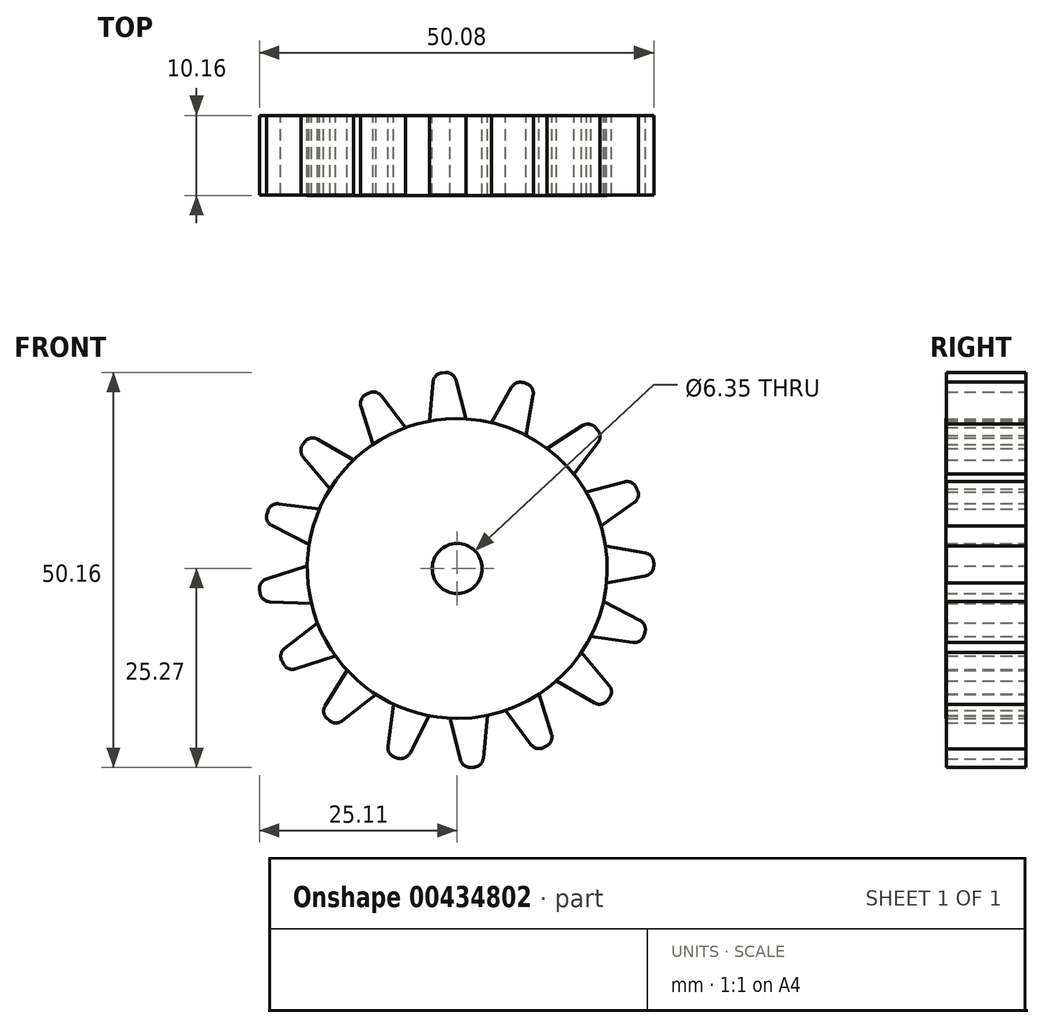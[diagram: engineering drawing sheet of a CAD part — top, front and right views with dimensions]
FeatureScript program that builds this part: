
annotation { "Feature Type Name" : "Feature", "Feature Type Description" : "" }
export const myFeature = defineFeature(function(context is Context, id is Id, definition is map)
    precondition{}
    {
        {
            var Q0;
            Q0=qCreatedBy(makeId("Front.planeOp"),FACE);
            var sketch = newSketch(context, id + "F0", { "sketchPlane" : qUnion([Q0])});
            skCircle(sketch, "E0", {"center": v(0, 0) * mm, "radius": 19.05 * mm});
            skCircle(sketch, "E1", {"center": v(0, 0) * mm, "radius": 3.18 * mm});
            skSolve(sketch);
        }
        {
            var Q0;
            Q0=makeQuery(id+"F0.imprint","IMPRINT",FACE,{"disambiguationData":[TD([[makeQuery(id+"F0.imprint","IMPRINT",EDGE,{"derivedFrom":sQuery(id+"F0.wireOp",EDGE,"E0")}),1.0]])]});
            extrude(context, id + "F1", {"entities" : qUnion([Q0]), "depth" : 3.8 * mm});
        }
        {
            var Q0;
            Q0=qCreatedBy(makeId("Front.planeOp"),FACE);
            var sketch = newSketch(context, id + "F2", { "sketchPlane" : qUnion([Q0])});
            skLineSegment(sketch, "E2", {"start": v(-45.5, 8.34) * mm, "end": v(-40.37, 8.34) * mm});
            skLineSegment(sketch, "E3", {"start": v(-45.5, 8.34) * mm, "end": v(-44.39, 14.6) * mm});
            skLineSegment(sketch, "E4", {"start": v(-43.14, 15.66) * mm, "end": v(-42.73, 15.66) * mm});
            skLineSegment(sketch, "E5", {"start": v(-41.48, 14.6) * mm, "end": v(-40.37, 8.34) * mm});
            skArc(sketch, "E6.filletArc", {"start": v(-43.14, 15.66) * mm, "mid": v(-43.95, 15.36) * mm, "end": v(-44.39, 14.6) * mm});
            skArc(sketch, "E7.filletArc", {"start": v(-41.48, 14.6) * mm, "mid": v(-41.91, 15.36) * mm, "end": v(-42.73, 15.66) * mm});
            skLineSegment(sketch, "E8", {"start": v(15.21, -9.97) * mm, "end": v(11.92, -13.9) * mm});
            skLineSegment(sketch, "E9", {"start": v(15.21, -9.97) * mm, "end": v(19.3, -14.84) * mm});
            skLineSegment(sketch, "E10", {"start": v(19.3, -16.48) * mm, "end": v(19.04, -16.8) * mm});
            skLineSegment(sketch, "E11", {"start": v(17.43, -17.07) * mm, "end": v(11.92, -13.9) * mm});
            skArc(sketch, "E12.filletArc", {"start": v(19.3, -16.48) * mm, "mid": v(19.6, -15.66) * mm, "end": v(19.3, -14.84) * mm});
            skArc(sketch, "E13.filletArc", {"start": v(17.43, -17.07) * mm, "mid": v(18.28, -17.23) * mm, "end": v(19.04, -16.8) * mm});
            skLineSegment(sketch, "E14", {"start": v(10.12, -14.98) * mm, "end": v(5.56, -17.3) * mm});
            skLineSegment(sketch, "E15", {"start": v(10.12, -14.98) * mm, "end": v(11.98, -21.06) * mm});
            skLineSegment(sketch, "E16", {"start": v(11.35, -22.56) * mm, "end": v(10.98, -22.75) * mm});
            skLineSegment(sketch, "E17", {"start": v(9.39, -22.38) * mm, "end": v(5.56, -17.3) * mm});
            skArc(sketch, "E18.filletArc", {"start": v(11.35, -22.56) * mm, "mid": v(11.94, -21.93) * mm, "end": v(11.98, -21.06) * mm});
            skArc(sketch, "E19.filletArc", {"start": v(9.39, -22.38) * mm, "mid": v(10.12, -22.85) * mm, "end": v(10.98, -22.75) * mm});
            skLineSegment(sketch, "E20", {"start": v(3.96, -17.77) * mm, "end": v(-1.15, -18.15) * mm});
            skLineSegment(sketch, "E21", {"start": v(3.96, -17.77) * mm, "end": v(3.32, -24.1) * mm});
            skLineSegment(sketch, "E22", {"start": v(2.15, -25.24) * mm, "end": v(1.74, -25.27) * mm});
            skLineSegment(sketch, "E23", {"start": v(0.42, -24.32) * mm, "end": v(-1.15, -18.15) * mm});
            skArc(sketch, "E24.filletArc", {"start": v(2.15, -25.24) * mm, "mid": v(2.95, -24.88) * mm, "end": v(3.32, -24.1) * mm});
            skArc(sketch, "E25.filletArc", {"start": v(0.42, -24.32) * mm, "mid": v(0.9, -25.04) * mm, "end": v(1.74, -25.27) * mm});
            skLineSegment(sketch, "E26", {"start": v(-3.1, -17.82) * mm, "end": v(-7.99, -16.3) * mm});
            skLineSegment(sketch, "E27", {"start": v(-3.1, -17.82) * mm, "end": v(-6.02, -23.47) * mm});
            skLineSegment(sketch, "E28", {"start": v(-7.53, -24.1) * mm, "end": v(-7.92, -23.98) * mm});
            skLineSegment(sketch, "E29", {"start": v(-8.8, -22.6) * mm, "end": v(-7.99, -16.3) * mm});
            skArc(sketch, "E30.filletArc", {"start": v(-7.53, -24.1) * mm, "mid": v(-6.66, -24.06) * mm, "end": v(-6.02, -23.47) * mm});
            skArc(sketch, "E31.filletArc", {"start": v(-8.8, -22.6) * mm, "mid": v(-8.61, -23.45) * mm, "end": v(-7.92, -23.98) * mm});
            skLineSegment(sketch, "E32", {"start": v(-9.59, -15.47) * mm, "end": v(-13.39, -12.04) * mm});
            skLineSegment(sketch, "E33", {"start": v(-9.59, -15.47) * mm, "end": v(-14.6, -19.38) * mm});
            skLineSegment(sketch, "E34", {"start": v(-16.24, -19.32) * mm, "end": v(-16.54, -19.04) * mm});
            skLineSegment(sketch, "E35", {"start": v(-16.77, -17.43) * mm, "end": v(-13.39, -12.04) * mm});
            skArc(sketch, "E36.filletArc", {"start": v(-16.24, -19.32) * mm, "mid": v(-15.44, -19.64) * mm, "end": v(-14.6, -19.38) * mm});
            skArc(sketch, "E37.filletArc", {"start": v(-16.77, -17.43) * mm, "mid": v(-16.95, -18.28) * mm, "end": v(-16.54, -19.04) * mm});
            skLineSegment(sketch, "E38", {"start": v(-14.5, -10.8) * mm, "end": v(-16.9, -6.27) * mm});
            skLineSegment(sketch, "E39", {"start": v(-14.5, -10.8) * mm, "end": v(-20.57, -12.74) * mm});
            skLineSegment(sketch, "E40", {"start": v(-22.08, -12.13) * mm, "end": v(-22.27, -11.77) * mm});
            skLineSegment(sketch, "E41", {"start": v(-21.93, -10.17) * mm, "end": v(-16.9, -6.27) * mm});
            skArc(sketch, "E42.filletArc", {"start": v(-22.08, -12.13) * mm, "mid": v(-21.43, -12.71) * mm, "end": v(-20.57, -12.74) * mm});
            skArc(sketch, "E43.filletArc", {"start": v(-21.93, -10.17) * mm, "mid": v(-22.39, -10.9) * mm, "end": v(-22.27, -11.77) * mm});
            skLineSegment(sketch, "E44", {"start": v(-17.48, -4.48) * mm, "end": v(-18.16, 0.6) * mm});
            skLineSegment(sketch, "E45", {"start": v(-17.48, -4.48) * mm, "end": v(-23.84, -4.22) * mm});
            skLineSegment(sketch, "E46", {"start": v(-25.04, -3.12) * mm, "end": v(-25.1, -2.71) * mm});
            skLineSegment(sketch, "E47", {"start": v(-24.22, -1.33) * mm, "end": v(-18.16, 0.6) * mm});
            skArc(sketch, "E48.filletArc", {"start": v(-25.04, -3.12) * mm, "mid": v(-24.64, -3.89) * mm, "end": v(-23.84, -4.22) * mm});
            skArc(sketch, "E49.filletArc", {"start": v(-24.22, -1.33) * mm, "mid": v(-24.91, -1.87) * mm, "end": v(-25.1, -2.71) * mm});
            skLineSegment(sketch, "E50", {"start": v(-17.87, 2.55) * mm, "end": v(-16.37, 7.44) * mm});
            skLineSegment(sketch, "E51", {"start": v(-17.87, 2.55) * mm, "end": v(-23.54, 5.44) * mm});
            skLineSegment(sketch, "E52", {"start": v(-24.17, 6.94) * mm, "end": v(-24.05, 7.33) * mm});
            skLineSegment(sketch, "E53", {"start": v(-22.68, 8.22) * mm, "end": v(-16.37, 7.44) * mm});
            skArc(sketch, "E54.filletArc", {"start": v(-24.17, 6.94) * mm, "mid": v(-24.13, 6.07) * mm, "end": v(-23.54, 5.44) * mm});
            skArc(sketch, "E55.filletArc", {"start": v(-22.68, 8.22) * mm, "mid": v(-23.53, 8.03) * mm, "end": v(-24.05, 7.33) * mm});
            skLineSegment(sketch, "E56", {"start": v(-15.47, 9.32) * mm, "end": v(-12.18, 13.24) * mm});
            skLineSegment(sketch, "E57", {"start": v(-15.47, 9.32) * mm, "end": v(-19.56, 14.2) * mm});
            skLineSegment(sketch, "E58", {"start": v(-19.56, 15.82) * mm, "end": v(-19.3, 16.14) * mm});
            skLineSegment(sketch, "E59", {"start": v(-17.7, 16.42) * mm, "end": v(-12.18, 13.24) * mm});
            skArc(sketch, "E60.filletArc", {"start": v(-19.56, 15.82) * mm, "mid": v(-19.86, 15) * mm, "end": v(-19.56, 14.2) * mm});
            skArc(sketch, "E61.filletArc", {"start": v(-17.7, 16.42) * mm, "mid": v(-18.55, 16.57) * mm, "end": v(-19.3, 16.14) * mm});
            skLineSegment(sketch, "E62", {"start": v(-10.32, 14.51) * mm, "end": v(-5.78, 16.86) * mm});
            skLineSegment(sketch, "E63", {"start": v(-10.32, 14.51) * mm, "end": v(-12.22, 20.58) * mm});
            skLineSegment(sketch, "E64", {"start": v(-11.6, 22.09) * mm, "end": v(-11.23, 22.28) * mm});
            skLineSegment(sketch, "E65", {"start": v(-9.64, 21.92) * mm, "end": v(-5.78, 16.86) * mm});
            skArc(sketch, "E66.filletArc", {"start": v(-11.6, 22.09) * mm, "mid": v(-12.18, 21.45) * mm, "end": v(-12.22, 20.58) * mm});
            skArc(sketch, "E67.filletArc", {"start": v(-9.64, 21.92) * mm, "mid": v(-10.37, 22.39) * mm, "end": v(-11.23, 22.28) * mm});
            skLineSegment(sketch, "E68", {"start": v(-3.63, 17.36) * mm, "end": v(1.47, 17.8) * mm});
            skLineSegment(sketch, "E69", {"start": v(-3.63, 17.36) * mm, "end": v(-3.08, 23.7) * mm});
            skLineSegment(sketch, "E70", {"start": v(-1.92, 24.85) * mm, "end": v(-1.52, 24.88) * mm});
            skLineSegment(sketch, "E71", {"start": v(-0.18, 23.95) * mm, "end": v(1.47, 17.8) * mm});
            skArc(sketch, "E72.filletArc", {"start": v(-1.92, 24.85) * mm, "mid": v(-2.71, 24.48) * mm, "end": v(-3.08, 23.7) * mm});
            skArc(sketch, "E73.filletArc", {"start": v(-0.18, 23.95) * mm, "mid": v(-0.68, 24.66) * mm, "end": v(-1.52, 24.88) * mm});
            skLineSegment(sketch, "E74", {"start": v(3.74, 17.53) * mm, "end": v(8.55, 15.78) * mm});
            skLineSegment(sketch, "E75", {"start": v(3.74, 17.53) * mm, "end": v(6.92, 23.04) * mm});
            skLineSegment(sketch, "E76", {"start": v(8.45, 23.6) * mm, "end": v(8.84, 23.46) * mm});
            skLineSegment(sketch, "E77", {"start": v(9.65, 22.04) * mm, "end": v(8.55, 15.78) * mm});
            skArc(sketch, "E78.filletArc", {"start": v(8.45, 23.6) * mm, "mid": v(7.58, 23.6) * mm, "end": v(6.92, 23.04) * mm});
            skArc(sketch, "E79.filletArc", {"start": v(9.65, 22.04) * mm, "mid": v(9.5, 22.9) * mm, "end": v(8.84, 23.46) * mm});
            skLineSegment(sketch, "E80", {"start": v(10.55, 14.73) * mm, "end": v(14, 10.95) * mm});
            skLineSegment(sketch, "E81", {"start": v(10.55, 14.73) * mm, "end": v(15.92, 18.14) * mm});
            skLineSegment(sketch, "E82", {"start": v(17.54, 17.93) * mm, "end": v(17.81, 17.63) * mm});
            skLineSegment(sketch, "E83", {"start": v(17.88, 16) * mm, "end": v(14, 10.95) * mm});
            skArc(sketch, "E84.filletArc", {"start": v(17.54, 17.93) * mm, "mid": v(16.77, 18.33) * mm, "end": v(15.92, 18.14) * mm});
            skArc(sketch, "E85.filletArc", {"start": v(17.88, 16) * mm, "mid": v(18.14, 16.82) * mm, "end": v(17.81, 17.63) * mm});
            skLineSegment(sketch, "E86", {"start": v(15.1, 9.35) * mm, "end": v(17.27, 4.71) * mm});
            skLineSegment(sketch, "E87", {"start": v(15.1, 9.35) * mm, "end": v(21.26, 11) * mm});
            skLineSegment(sketch, "E88", {"start": v(22.73, 10.31) * mm, "end": v(22.9, 9.94) * mm});
            skLineSegment(sketch, "E89", {"start": v(22.49, 8.36) * mm, "end": v(17.27, 4.71) * mm});
            skArc(sketch, "E90.filletArc", {"start": v(22.73, 10.31) * mm, "mid": v(22.12, 10.93) * mm, "end": v(21.26, 11) * mm});
            skArc(sketch, "E91.filletArc", {"start": v(22.49, 8.36) * mm, "mid": v(22.98, 9.07) * mm, "end": v(22.9, 9.94) * mm});
            skLineSegment(sketch, "E92", {"start": v(17.65, 3.08) * mm, "end": v(17.65, -2.04) * mm});
            skLineSegment(sketch, "E93", {"start": v(17.65, 3.08) * mm, "end": v(23.92, 1.97) * mm});
            skLineSegment(sketch, "E94", {"start": v(24.97, 0.72) * mm, "end": v(24.97, 0.31) * mm});
            skLineSegment(sketch, "E95", {"start": v(23.92, -0.94) * mm, "end": v(17.65, -2.04) * mm});
            skArc(sketch, "E96.filletArc", {"start": v(24.97, 0.72) * mm, "mid": v(24.67, 1.54) * mm, "end": v(23.92, 1.97) * mm});
            skArc(sketch, "E97.filletArc", {"start": v(23.92, -0.94) * mm, "mid": v(24.67, -0.5) * mm, "end": v(24.97, 0.31) * mm});
            skLineSegment(sketch, "E98", {"start": v(17.6, -3.64) * mm, "end": v(16.04, -8.51) * mm});
            skLineSegment(sketch, "E99", {"start": v(17.6, -3.64) * mm, "end": v(23.23, -6.6) * mm});
            skLineSegment(sketch, "E100", {"start": v(23.85, -8.12) * mm, "end": v(23.72, -8.51) * mm});
            skLineSegment(sketch, "E101", {"start": v(22.34, -9.38) * mm, "end": v(16.04, -8.51) * mm});
            skArc(sketch, "E102.filletArc", {"start": v(23.85, -8.12) * mm, "mid": v(23.81, -7.25) * mm, "end": v(23.23, -6.6) * mm});
            skArc(sketch, "E103.filletArc", {"start": v(22.34, -9.38) * mm, "mid": v(23.19, -9.2) * mm, "end": v(23.72, -8.51) * mm});
            skSolve(sketch);
        }
        {
            var Q0;
            Q0 = qSketchRegion(id + "F2", true);
            extrude(context, id + "F3", {"entities" : qUnion([Q0]), "operationType" : NewBodyOperationType.ADD, "depth" : 3.73 * mm});
        }
        {
            var Q0;
            Q0=makeQuery(id+"F3.opExtrude","SWEPT_BODY",BODY,{"disambiguationData":[OSD([sQuery(id+"F2.wireOp",EDGE,"E2"),sQuery(id+"F2.wireOp",EDGE,"E3"),sQuery(id+"F2.wireOp",EDGE,"E4"),sQuery(id+"F2.wireOp",EDGE,"E5"),sQuery(id+"F2.wireOp",EDGE,"E6.filletArc"),sQuery(id+"F2.wireOp",EDGE,"E7.filletArc")])]});
            deleteBodies(context, id + "F4", {"entities" : qUnion([Q0])});
        }
        {
            var Q0;
            Q0=makeQuery(id+"F1.opExtrude","CAP_FACE",FACE,{"disambiguationData":[OSD([sQuery(id+"F0.wireOp",EDGE,"E0"),sQuery(id+"F0.wireOp",EDGE,"E1")])],"isStart":false});
            extrude(context, id + "F5", {"entities" : qUnion([Q0]), "operationType" : NewBodyOperationType.ADD, "depth" : 6.35 * mm});
        }
        {
            var Q0;
            Q0=makeQuery(id+"F3.boolean.opBoolean","MERGE",FACE,{"derivedFrom":[makeQuery(id+"F1.opExtrude","CAP_FACE",FACE,{"disambiguationData":[OSD([sQuery(id+"F0.wireOp",EDGE,"E0"),sQuery(id+"F0.wireOp",EDGE,"E1")])],"isStart":true}),makeQuery(id+"F3.opExtrude","CAP_FACE",FACE,{"disambiguationData":[OSD([sQuery(id+"F2.wireOp",EDGE,"E8"),sQuery(id+"F2.wireOp",EDGE,"E9"),sQuery(id+"F2.wireOp",EDGE,"E10"),sQuery(id+"F2.wireOp",EDGE,"E11"),sQuery(id+"F2.wireOp",EDGE,"E12.filletArc"),sQuery(id+"F2.wireOp",EDGE,"E13.filletArc")])],"isStart":true}),makeQuery(id+"F3.opExtrude","CAP_FACE",FACE,{"disambiguationData":[OSD([sQuery(id+"F2.wireOp",EDGE,"E14"),sQuery(id+"F2.wireOp",EDGE,"E15"),sQuery(id+"F2.wireOp",EDGE,"E16"),sQuery(id+"F2.wireOp",EDGE,"E17"),sQuery(id+"F2.wireOp",EDGE,"E18.filletArc"),sQuery(id+"F2.wireOp",EDGE,"E19.filletArc")])],"isStart":true}),makeQuery(id+"F3.opExtrude","CAP_FACE",FACE,{"disambiguationData":[OSD([sQuery(id+"F2.wireOp",EDGE,"E20"),sQuery(id+"F2.wireOp",EDGE,"E21"),sQuery(id+"F2.wireOp",EDGE,"E22"),sQuery(id+"F2.wireOp",EDGE,"E23"),sQuery(id+"F2.wireOp",EDGE,"E24.filletArc"),sQuery(id+"F2.wireOp",EDGE,"E25.filletArc")])],"isStart":true}),makeQuery(id+"F3.opExtrude","CAP_FACE",FACE,{"disambiguationData":[OSD([sQuery(id+"F2.wireOp",EDGE,"E26"),sQuery(id+"F2.wireOp",EDGE,"E27"),sQuery(id+"F2.wireOp",EDGE,"E28"),sQuery(id+"F2.wireOp",EDGE,"E29"),sQuery(id+"F2.wireOp",EDGE,"E30.filletArc"),sQuery(id+"F2.wireOp",EDGE,"E31.filletArc")])],"isStart":true}),makeQuery(id+"F3.opExtrude","CAP_FACE",FACE,{"disambiguationData":[OSD([sQuery(id+"F2.wireOp",EDGE,"E32"),sQuery(id+"F2.wireOp",EDGE,"E33"),sQuery(id+"F2.wireOp",EDGE,"E34"),sQuery(id+"F2.wireOp",EDGE,"E35"),sQuery(id+"F2.wireOp",EDGE,"E36.filletArc"),sQuery(id+"F2.wireOp",EDGE,"E37.filletArc")])],"isStart":true}),makeQuery(id+"F3.opExtrude","CAP_FACE",FACE,{"disambiguationData":[OSD([sQuery(id+"F2.wireOp",EDGE,"E38"),sQuery(id+"F2.wireOp",EDGE,"E39"),sQuery(id+"F2.wireOp",EDGE,"E40"),sQuery(id+"F2.wireOp",EDGE,"E41"),sQuery(id+"F2.wireOp",EDGE,"E42.filletArc"),sQuery(id+"F2.wireOp",EDGE,"E43.filletArc")])],"isStart":true}),makeQuery(id+"F3.opExtrude","CAP_FACE",FACE,{"disambiguationData":[OSD([sQuery(id+"F2.wireOp",EDGE,"E44"),sQuery(id+"F2.wireOp",EDGE,"E45"),sQuery(id+"F2.wireOp",EDGE,"E46"),sQuery(id+"F2.wireOp",EDGE,"E47"),sQuery(id+"F2.wireOp",EDGE,"E48.filletArc"),sQuery(id+"F2.wireOp",EDGE,"E49.filletArc")])],"isStart":true}),makeQuery(id+"F3.opExtrude","CAP_FACE",FACE,{"disambiguationData":[OSD([sQuery(id+"F2.wireOp",EDGE,"E50"),sQuery(id+"F2.wireOp",EDGE,"E51"),sQuery(id+"F2.wireOp",EDGE,"E52"),sQuery(id+"F2.wireOp",EDGE,"E53"),sQuery(id+"F2.wireOp",EDGE,"E54.filletArc"),sQuery(id+"F2.wireOp",EDGE,"E55.filletArc")])],"isStart":true}),makeQuery(id+"F3.opExtrude","CAP_FACE",FACE,{"disambiguationData":[OSD([sQuery(id+"F2.wireOp",EDGE,"E56"),sQuery(id+"F2.wireOp",EDGE,"E57"),sQuery(id+"F2.wireOp",EDGE,"E58"),sQuery(id+"F2.wireOp",EDGE,"E59"),sQuery(id+"F2.wireOp",EDGE,"E60.filletArc"),sQuery(id+"F2.wireOp",EDGE,"E61.filletArc")])],"isStart":true}),makeQuery(id+"F3.opExtrude","CAP_FACE",FACE,{"disambiguationData":[OSD([sQuery(id+"F2.wireOp",EDGE,"E62"),sQuery(id+"F2.wireOp",EDGE,"E63"),sQuery(id+"F2.wireOp",EDGE,"E64"),sQuery(id+"F2.wireOp",EDGE,"E65"),sQuery(id+"F2.wireOp",EDGE,"E66.filletArc"),sQuery(id+"F2.wireOp",EDGE,"E67.filletArc")])],"isStart":true}),makeQuery(id+"F3.opExtrude","CAP_FACE",FACE,{"disambiguationData":[OSD([sQuery(id+"F2.wireOp",EDGE,"E68"),sQuery(id+"F2.wireOp",EDGE,"E69"),sQuery(id+"F2.wireOp",EDGE,"E70"),sQuery(id+"F2.wireOp",EDGE,"E71"),sQuery(id+"F2.wireOp",EDGE,"E72.filletArc"),sQuery(id+"F2.wireOp",EDGE,"E73.filletArc")])],"isStart":true}),makeQuery(id+"F3.opExtrude","CAP_FACE",FACE,{"disambiguationData":[OSD([sQuery(id+"F2.wireOp",EDGE,"E74"),sQuery(id+"F2.wireOp",EDGE,"E75"),sQuery(id+"F2.wireOp",EDGE,"E76"),sQuery(id+"F2.wireOp",EDGE,"E77"),sQuery(id+"F2.wireOp",EDGE,"E78.filletArc"),sQuery(id+"F2.wireOp",EDGE,"E79.filletArc")])],"isStart":true}),makeQuery(id+"F3.opExtrude","CAP_FACE",FACE,{"disambiguationData":[OSD([sQuery(id+"F2.wireOp",EDGE,"E80"),sQuery(id+"F2.wireOp",EDGE,"E81"),sQuery(id+"F2.wireOp",EDGE,"E82"),sQuery(id+"F2.wireOp",EDGE,"E83"),sQuery(id+"F2.wireOp",EDGE,"E84.filletArc"),sQuery(id+"F2.wireOp",EDGE,"E85.filletArc")])],"isStart":true}),makeQuery(id+"F3.opExtrude","CAP_FACE",FACE,{"disambiguationData":[OSD([sQuery(id+"F2.wireOp",EDGE,"E86"),sQuery(id+"F2.wireOp",EDGE,"E87"),sQuery(id+"F2.wireOp",EDGE,"E88"),sQuery(id+"F2.wireOp",EDGE,"E89"),sQuery(id+"F2.wireOp",EDGE,"E90.filletArc"),sQuery(id+"F2.wireOp",EDGE,"E91.filletArc")])],"isStart":true}),makeQuery(id+"F3.opExtrude","CAP_FACE",FACE,{"disambiguationData":[OSD([sQuery(id+"F2.wireOp",EDGE,"E92"),sQuery(id+"F2.wireOp",EDGE,"E93"),sQuery(id+"F2.wireOp",EDGE,"E94"),sQuery(id+"F2.wireOp",EDGE,"E95"),sQuery(id+"F2.wireOp",EDGE,"E96.filletArc"),sQuery(id+"F2.wireOp",EDGE,"E97.filletArc")])],"isStart":true}),makeQuery(id+"F3.opExtrude","CAP_FACE",FACE,{"disambiguationData":[OSD([sQuery(id+"F2.wireOp",EDGE,"E98"),sQuery(id+"F2.wireOp",EDGE,"E99"),sQuery(id+"F2.wireOp",EDGE,"E100"),sQuery(id+"F2.wireOp",EDGE,"E101"),sQuery(id+"F2.wireOp",EDGE,"E102.filletArc"),sQuery(id+"F2.wireOp",EDGE,"E103.filletArc")])],"isStart":true})]});
            extrude(context, id + "F6", {"entities" : qUnion([Q0]), "operationType" : NewBodyOperationType.ADD, "oppositeDirection" : true, "depth" : 10.1 * mm});
        }
    });
